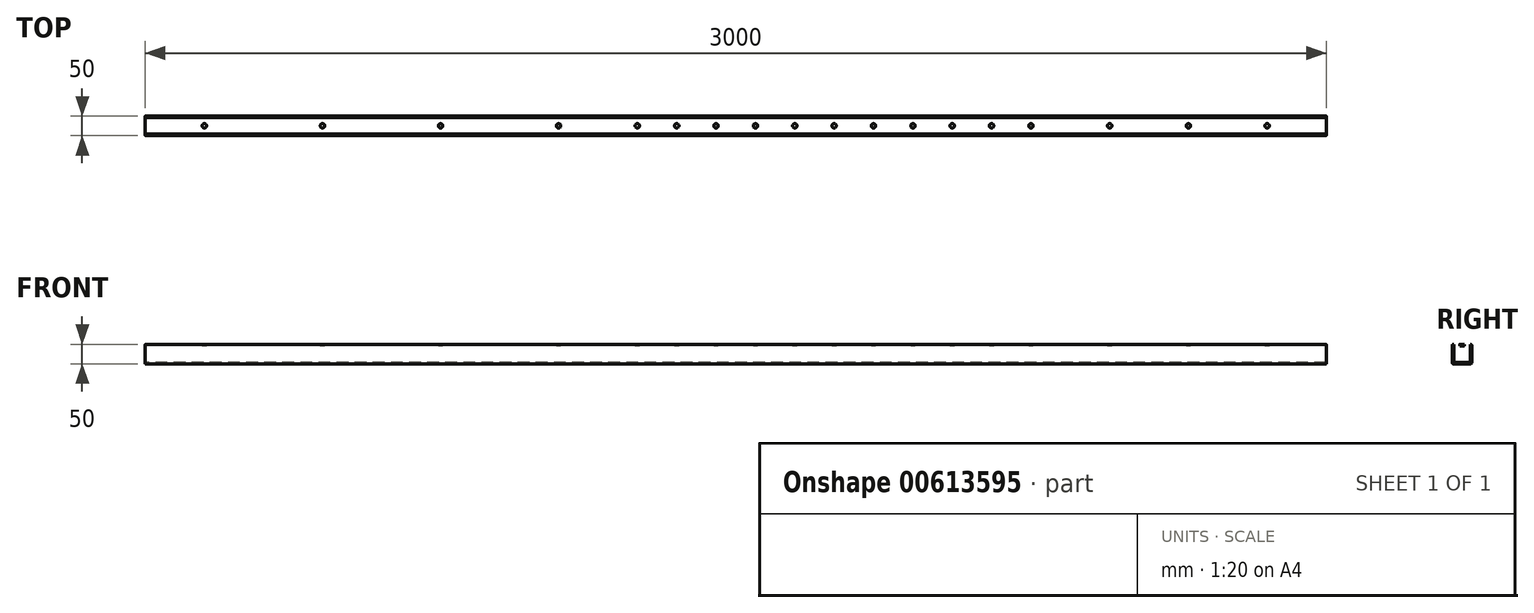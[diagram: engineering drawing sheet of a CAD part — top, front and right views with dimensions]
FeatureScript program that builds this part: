
annotation { "Feature Type Name" : "Feature", "Feature Type Description" : "" }
export const myFeature = defineFeature(function(context is Context, id is Id, definition is map)
    precondition{}
    {
        {
            var Q0;
            Q0=qCreatedBy(makeId("Right.planeOp"),FACE);
            var sketch = newSketch(context, id + "F0", { "sketchPlane" : qUnion([Q0])});
            skLineSegment(sketch, "E0.bottom", {"start": v(4, 0) * mm, "end": v(46, 0) * mm});
            skLineSegment(sketch, "E0.top", {"start": v(4, 50) * mm, "end": v(46, 50) * mm});
            skLineSegment(sketch, "E0.left", {"start": v(0, 4) * mm, "end": v(0, 46) * mm});
            skLineSegment(sketch, "E0.right", {"start": v(50, 4) * mm, "end": v(50, 46) * mm});
            skLineSegment(sketch, "E1.0", {"start": v(4, 46) * mm, "end": v(46, 46) * mm});
            skLineSegment(sketch, "E1.1", {"start": v(4, 4) * mm, "end": v(4, 46) * mm});
            skLineSegment(sketch, "E1.2", {"start": v(4, 4) * mm, "end": v(46, 4) * mm});
            skLineSegment(sketch, "E1.3", {"start": v(46, 4) * mm, "end": v(46, 46) * mm});
            skPoint(sketch, "E2.visualSharp", {"position": v(0, 50) * mm});
            skArc(sketch, "E2.filletArc", {"start": v(4, 50) * mm, "mid": v(1.17, 48.83) * mm, "end": v(0, 46) * mm});
            skPoint(sketch, "E3.visualSharp", {"position": v(50, 50) * mm});
            skArc(sketch, "E3.filletArc", {"start": v(50, 46) * mm, "mid": v(48.83, 48.83) * mm, "end": v(46, 50) * mm});
            skPoint(sketch, "E4.visualSharp", {"position": v(50, 0) * mm});
            skArc(sketch, "E4.filletArc", {"start": v(46, 0) * mm, "mid": v(48.83, 1.17) * mm, "end": v(50, 4) * mm});
            skPoint(sketch, "E5.visualSharp", {"position": v(0, 0) * mm});
            skArc(sketch, "E5.filletArc", {"start": v(0, 4) * mm, "mid": v(1.17, 1.17) * mm, "end": v(4, 0) * mm});
            skSolve(sketch);
        }
        {
            var Q0;
            Q0=makeQuery(id+"F0.imprint","IMPRINT",FACE,{"disambiguationData":[TD([[makeQuery(id+"F0.imprint","IMPRINT",EDGE,{"derivedFrom":sQuery(id+"F0.wireOp",EDGE,"E0.bottom")}),1.0]])]});
            extrude(context, id + "F1", {"entities" : qUnion([Q0]), "depth" : 3000 * mm, "offsetDistance" : 25 * mm});
        }
        {
            var Q0;
            Q0=makeQuery(id+"F1.opExtrude","SWEPT_FACE",FACE,{"disambiguationData":[OSD([sQuery(id+"F0.wireOp",EDGE,"E0.top")])]});
            var sketch = newSketch(context, id + "F2", { "sketchPlane" : qUnion([Q0])});
            skCircle(sketch, "E6.MirrorC", {"center": v(450, 25) * mm, "radius": 5.5 * mm});
            skCircle(sketch, "E7.MirrorC", {"center": v(150, 25) * mm, "radius": 5.5 * mm});
            skCircle(sketch, "E8.MirrorC", {"center": v(1450, 25) * mm, "radius": 5.5 * mm});
            skCircle(sketch, "E9.MirrorC", {"center": v(1550, 25) * mm, "radius": 5.5 * mm});
            skCircle(sketch, "E10.MirrorC", {"center": v(1650, 25) * mm, "radius": 5.5 * mm});
            skCircle(sketch, "E11.MirrorC", {"center": v(1750, 25) * mm, "radius": 5.5 * mm});
            skCircle(sketch, "E12.MirrorC", {"center": v(2450, 25) * mm, "radius": 5.5 * mm});
            skCircle(sketch, "E13.MirrorC", {"center": v(2150, 25) * mm, "radius": 5.5 * mm});
            skCircle(sketch, "E14.MirrorC", {"center": v(2650, 25) * mm, "radius": 5.5 * mm});
            skCircle(sketch, "E15.MirrorC", {"center": v(2250, 25) * mm, "radius": 5.5 * mm});
            skCircle(sketch, "E16.MirrorC", {"center": v(1850, 25) * mm, "radius": 5.5 * mm});
            skCircle(sketch, "E17.MirrorC", {"center": v(1950, 25) * mm, "radius": 5.5 * mm});
            skCircle(sketch, "E18.MirrorC", {"center": v(2050, 25) * mm, "radius": 5.5 * mm});
            skCircle(sketch, "E19.MirrorC", {"center": v(2850, 25) * mm, "radius": 5.5 * mm});
            skCircle(sketch, "E20.MirrorC", {"center": v(1350, 25) * mm, "radius": 5.5 * mm});
            skCircle(sketch, "E21.MirrorC", {"center": v(1250, 25) * mm, "radius": 5.5 * mm});
            skCircle(sketch, "E22.MirrorC", {"center": v(750, 25) * mm, "radius": 5.5 * mm});
            skCircle(sketch, "E23.MirrorC", {"center": v(1050, 25) * mm, "radius": 5.5 * mm});
            skLineSegment(sketch, "E24.bottom", {"start": v(3000, 0) * mm, "end": v(0, 0) * mm, "construction": true});
            skLineSegment(sketch, "E24.top", {"start": v(3000, 50) * mm, "end": v(0, 50) * mm, "construction": true});
            skLineSegment(sketch, "E24.left", {"start": v(3000, 0) * mm, "end": v(3000, 50) * mm, "construction": true});
            skLineSegment(sketch, "E24.right", {"start": v(0, 0) * mm, "end": v(0, 50) * mm, "construction": true});
            skSolve(sketch);
        }
        {
            var Q0;
            Q0=makeQuery(id+"F2.imprint","IMPRINT",FACE,{"disambiguationData":[TD([[makeQuery(id+"F2.imprint","IMPRINT",EDGE,{"derivedFrom":sQuery(id+"F2.wireOp",EDGE,"E7.MirrorC")}),-1.0]])]});
            var Q1;
            Q1=makeQuery(id+"F2.imprint","IMPRINT",FACE,{"disambiguationData":[TD([[makeQuery(id+"F2.imprint","IMPRINT",EDGE,{"derivedFrom":sQuery(id+"F2.wireOp",EDGE,"E6.MirrorC")}),-1.0]])]});
            var Q2;
            Q2=makeQuery(id+"F2.imprint","IMPRINT",FACE,{"disambiguationData":[TD([[makeQuery(id+"F2.imprint","IMPRINT",EDGE,{"derivedFrom":sQuery(id+"F2.wireOp",EDGE,"E22.MirrorC")}),-1.0]])]});
            var Q3;
            Q3=makeQuery(id+"F2.imprint","IMPRINT",FACE,{"disambiguationData":[TD([[makeQuery(id+"F2.imprint","IMPRINT",EDGE,{"derivedFrom":sQuery(id+"F2.wireOp",EDGE,"E23.MirrorC")}),-1.0]])]});
            var Q4;
            Q4=makeQuery(id+"F2.imprint","IMPRINT",FACE,{"disambiguationData":[TD([[makeQuery(id+"F2.imprint","IMPRINT",EDGE,{"derivedFrom":sQuery(id+"F2.wireOp",EDGE,"E21.MirrorC")}),-1.0]])]});
            var Q5;
            Q5=makeQuery(id+"F2.imprint","IMPRINT",FACE,{"disambiguationData":[TD([[makeQuery(id+"F2.imprint","IMPRINT",EDGE,{"derivedFrom":sQuery(id+"F2.wireOp",EDGE,"E20.MirrorC")}),-1.0]])]});
            var Q6;
            Q6=makeQuery(id+"F2.imprint","IMPRINT",FACE,{"disambiguationData":[TD([[makeQuery(id+"F2.imprint","IMPRINT",EDGE,{"derivedFrom":sQuery(id+"F2.wireOp",EDGE,"E9.MirrorC")}),-1.0]])]});
            var Q7;
            Q7=makeQuery(id+"F2.imprint","IMPRINT",FACE,{"disambiguationData":[TD([[makeQuery(id+"F2.imprint","IMPRINT",EDGE,{"derivedFrom":sQuery(id+"F2.wireOp",EDGE,"E8.MirrorC")}),-1.0]])]});
            var Q8;
            Q8=makeQuery(id+"F2.imprint","IMPRINT",FACE,{"disambiguationData":[TD([[makeQuery(id+"F2.imprint","IMPRINT",EDGE,{"derivedFrom":sQuery(id+"F2.wireOp",EDGE,"E10.MirrorC")}),-1.0]])]});
            var Q9;
            Q9=makeQuery(id+"F2.imprint","IMPRINT",FACE,{"disambiguationData":[TD([[makeQuery(id+"F2.imprint","IMPRINT",EDGE,{"derivedFrom":sQuery(id+"F2.wireOp",EDGE,"E11.MirrorC")}),-1.0]])]});
            var Q10;
            Q10=makeQuery(id+"F2.imprint","IMPRINT",FACE,{"disambiguationData":[TD([[makeQuery(id+"F2.imprint","IMPRINT",EDGE,{"derivedFrom":sQuery(id+"F2.wireOp",EDGE,"E16.MirrorC")}),-1.0]])]});
            var Q11;
            Q11=makeQuery(id+"F2.imprint","IMPRINT",FACE,{"disambiguationData":[TD([[makeQuery(id+"F2.imprint","IMPRINT",EDGE,{"derivedFrom":sQuery(id+"F2.wireOp",EDGE,"E17.MirrorC")}),-1.0]])]});
            var Q12;
            Q12=makeQuery(id+"F2.imprint","IMPRINT",FACE,{"disambiguationData":[TD([[makeQuery(id+"F2.imprint","IMPRINT",EDGE,{"derivedFrom":sQuery(id+"F2.wireOp",EDGE,"E18.MirrorC")}),-1.0]])]});
            var Q13;
            Q13=makeQuery(id+"F2.imprint","IMPRINT",FACE,{"disambiguationData":[TD([[makeQuery(id+"F2.imprint","IMPRINT",EDGE,{"derivedFrom":sQuery(id+"F2.wireOp",EDGE,"E13.MirrorC")}),-1.0]])]});
            var Q14;
            Q14=makeQuery(id+"F2.imprint","IMPRINT",FACE,{"disambiguationData":[TD([[makeQuery(id+"F2.imprint","IMPRINT",EDGE,{"derivedFrom":sQuery(id+"F2.wireOp",EDGE,"E15.MirrorC")}),-1.0]])]});
            var Q15;
            Q15=makeQuery(id+"F2.imprint","IMPRINT",FACE,{"disambiguationData":[TD([[makeQuery(id+"F2.imprint","IMPRINT",EDGE,{"derivedFrom":sQuery(id+"F2.wireOp",EDGE,"E12.MirrorC")}),-1.0]])]});
            var Q16;
            Q16=makeQuery(id+"F2.imprint","IMPRINT",FACE,{"disambiguationData":[TD([[makeQuery(id+"F2.imprint","IMPRINT",EDGE,{"derivedFrom":sQuery(id+"F2.wireOp",EDGE,"E14.MirrorC")}),-1.0]])]});
            var Q17;
            Q17=makeQuery(id+"F2.imprint","IMPRINT",FACE,{"disambiguationData":[TD([[makeQuery(id+"F2.imprint","IMPRINT",EDGE,{"derivedFrom":sQuery(id+"F2.wireOp",EDGE,"E19.MirrorC")}),-1.0]])]});
            var Q18;
            Q18=sQuery(id+"F2.wireOp",EDGE,"E24.top");
            var Q19;
            Q19=sQuery(id+"F2.wireOp",EDGE,"E24.right");
            var Q20;
            Q20=sQuery(id+"F2.wireOp",EDGE,"E24.bottom");
            var Q21;
            Q21=sQuery(id+"F2.wireOp",EDGE,"E24.left");
            extrude(context, id + "F3", {"entities" : qUnion([Q0, Q1, Q2, Q3, Q4, Q5, Q6, Q7, Q8, Q9, Q10, Q11, Q12, Q13, Q14, Q15, Q16, Q17]), "operationType" : NewBodyOperationType.REMOVE, "surfaceEntities" : qUnion([Q18, Q19, Q20, Q21]), "oppositeDirection" : true, "depth" : 25 * mm, "offsetDistance" : 25 * mm});
        }
    });
